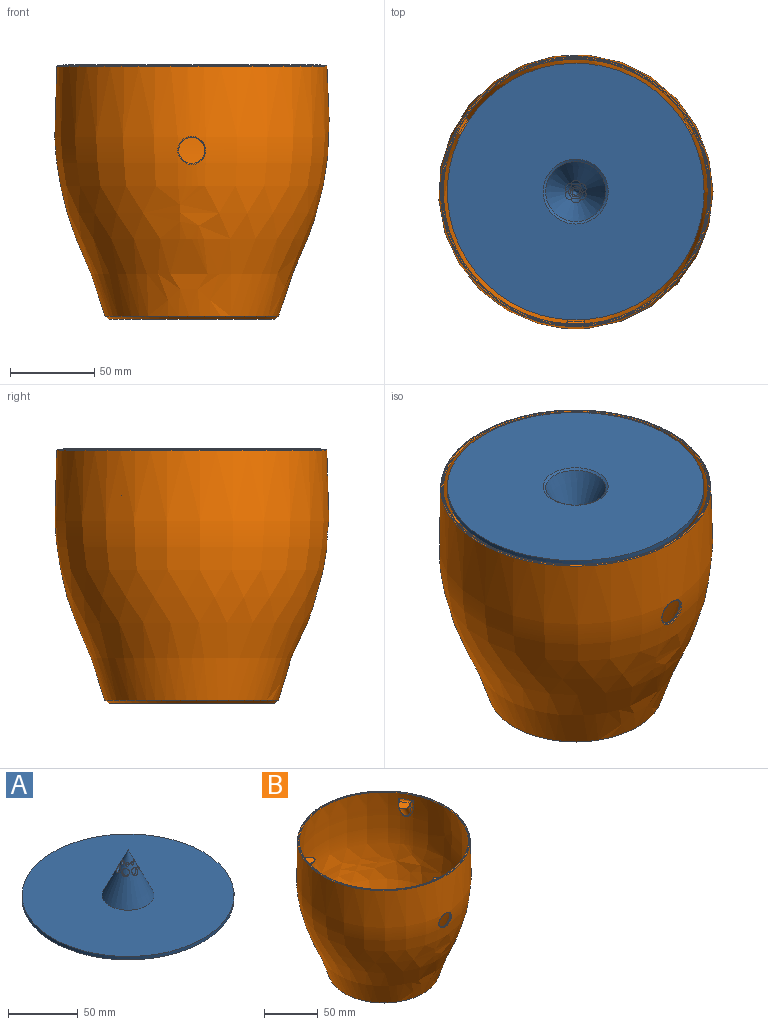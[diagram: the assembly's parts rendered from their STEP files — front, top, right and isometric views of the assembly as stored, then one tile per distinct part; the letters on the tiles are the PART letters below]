
ASSEMBLY  parts=2 mates=1
PART A: 25 faces, bbox 152x152x42.9 mm
  f0: cylinder r=2.75mm len=5.49mm, axis (0,1,0), area 15.8mm2, adj f1
  f1: cone r=18.55mm half-angle=25deg, axis (0,0,-1), area 27.1mm2, adj f0
  f2: cone r=18.55mm half-angle=25deg, axis (0,0,-1), area 2358.4mm2, adj f3
  f3: cone r=19.23mm half-angle=57.5deg, axis (0,0,-1), area 196.3mm2, adj f2,f4
  f4: plane 152.05x152.05mm, normal (0,0,1), area 16994.9mm2, adj f3,f5
  f5: cylinder r=76.02mm len=152.05mm, axis (0,0,-1), area 1433mm2, adj f4,f6
  f6: plane 152.05x152.05mm, normal (0,0,-1), area 17070.2mm2, adj f5,f7
  f7: cone r=20mm half-angle=25deg, axis (0,0,-1), area 2373.6mm2, adj f6,f8,f9,f13,f14,f15,f16,f17
  f8: cylinder r=2.75mm len=5.49mm, axis (0,1,0), area 48mm2, adj f7
  f9: cylinder r=2.75mm len=6.92mm, axis (-0.87,0.5,0), area 31.3mm2, adj f7,f10,f11,f12,f14
  f10: cone r=18.55mm half-angle=25deg, axis (0,0,-1), area 294.3mm2, adj f9,f11,f13,f14,f15,f16
  f11: cylinder r=2.75mm len=5.49mm, axis (0,1,0), area 16.5mm2, adj f9,f10,f12,f13
  f12: cone r=18.55mm half-angle=25deg, axis (0,0,-1), area 61.3mm2, adj f9,f11,f13,f14,f15,f16,f17,f19
  f13: cylinder r=2.75mm len=6.92mm, axis (-0.87,-0.5,0), area 31.3mm2, adj f7,f10,f11,f12,f16
  f14: cylinder r=2.75mm len=6.93mm, axis (-0.87,-0.5,0), area 31.4mm2, adj f7,f9,f10,f12,f15
  f15: cylinder r=2.75mm len=5.49mm, axis (0,-1,0), area 31.3mm2, adj f7,f10,f12,f14,f16
  f16: cylinder r=2.75mm len=6.92mm, axis (0.87,-0.5,0), area 31.3mm2, adj f7,f10,f12,f13,f15
  f17: cylinder r=1.25mm len=2.92mm, axis (0,1,0), area 14mm2, adj f7,f12,f18,f19,f20
  f18: cone r=18.55mm half-angle=25deg, axis (0,0,-1), area 34.9mm2, adj f17,f19,f20,f21,f22,f23,f24
  f19: cylinder r=1.25mm len=3.85mm, axis (-0.78,0.62,0), area 14mm2, adj f7,f12,f17,f18,f24
  f20: cylinder r=1.25mm len=3.85mm, axis (0.78,0.62,0), area 13.9mm2, adj f7,f12,f17,f18,f23
  f21: cylinder r=1.25mm len=3.72mm, axis (-0.43,-0.9,0), area 14mm2, adj f7,f12,f18,f22,f24
  f22: cylinder r=1.25mm len=3.72mm, axis (0.43,-0.9,0), area 14mm2, adj f7,f12,f18,f21,f23
  f23: cylinder r=1.25mm len=3.41mm, axis (0.97,-0.22,0), area 13.9mm2, adj f7,f12,f18,f20,f22
  f24: cylinder r=1.25mm len=3.43mm, axis (-0.97,-0.22,0), area 14mm2, adj f7,f12,f18,f19,f21
PART B: 39 faces, bbox 173.3x173.3x150 mm
  f0: revolved ~159.5x159.5mm, area 119611.4mm2, adj f21,f22,f23,f24,f25,f26,f27,f28
  f1: revolved ~162.68x162.68mm, area 69001.8mm2, adj f18,f19,f20
  f2: plane 97.7x97.7mm, normal (0,0,-1), area 7496.5mm2, adj f19
  f3: plane 159.07x159.07mm, normal (0,0,1), area 299.5mm2, adj f17,f18
  f4: cylinder r=7.75mm len=15.5mm, axis (0,1,0), area 29.4mm2, adj f20,f21
  f5: plane 10.71x10mm, normal (0,0,1), area 92.9mm2, adj f6,f7,f8,f31,f32,f33
  f6: plane 5.68x4.46mm, normal (1,0,0), area 11.8mm2, adj f5,f8,f32
  f7: plane 5.68x4.46mm, normal (-1,0,0), area 11.8mm2, adj f5,f8,f31
  f8: cylinder r=5mm len=19.8mm, axis (0,-0.62,-0.79), area 253mm2, adj f5,f6,f7,f30
  f9: plane 12.18x11.8mm, normal (0,0,1), area 92.9mm2, adj f10,f11,f12,f27,f28,f29
  f10: plane 5.68x3.86mm, normal (-0.5,0.87,0), area 11.8mm2, adj f9,f12,f28
  f11: plane 5.68x3.86mm, normal (0.5,-0.87,0), area 11.8mm2, adj f9,f12,f27
  f12: cylinder r=5mm len=19.8mm, axis (0.53,0.31,-0.79), area 253mm2, adj f9,f10,f11,f26
  f13: plane 12.18x11.8mm, normal (0,0,1), area 92.9mm2, adj f14,f15,f16,f23,f24,f25
  f14: plane 5.68x3.86mm, normal (-0.5,-0.87,0), area 11.8mm2, adj f13,f16,f24
  f15: plane 5.68x3.86mm, normal (0.5,0.87,0), area 11.8mm2, adj f13,f16,f23
  f16: cylinder r=5mm len=19.8mm, axis (-0.53,0.31,-0.79), area 253mm2, adj f13,f14,f15,f22
  f17: torus R=78.93mm, axis (0,0,1), area 405.9mm2, adj f3
  f18: torus R=79.54mm, axis (0,0,1), area 375.8mm2, adj f1,f3
  f19: cone r=51.43mm half-angle=53.4deg, axis (0,0,1), area 1011.9mm2, adj f1,f2
  f20: bspline ~16.63x16.55mm, area 41.1mm2, adj f1,f4
  f21: bspline ~16.48x16.41mm, area 37.3mm2, adj f0,f4
  f22: bspline ~14.57x12.47mm, area 64.1mm2, adj f0,f16,f23,f24
  f23: bspline ~23.78x3.41mm, area 21.3mm2, adj f0,f13,f15,f22,f25
  f24: bspline ~23.78x3.73mm, area 21.3mm2, adj f0,f13,f14,f22,f25
  f25: torus R=76.88mm, axis (0,0,1), area 38mm2, adj f0,f13,f23,f24
  f26: bspline ~14.57x12.46mm, area 64.1mm2, adj f0,f12,f27,f28
  f27: bspline ~23.78x3.73mm, area 21.3mm2, adj f0,f9,f11,f26,f29
  f28: bspline ~23.78x3.41mm, area 21.3mm2, adj f0,f9,f10,f26,f29
  f29: torus R=76.88mm, axis (0,0,1), area 38mm2, adj f0,f9,f27,f28
  f30: bspline ~14.57x14.36mm, area 64.1mm2, adj f0,f8,f31,f32
  f31: bspline ~23.78x3.25mm, area 21.3mm2, adj f0,f5,f7,f30,f33
  f32: bspline ~23.78x3.25mm, area 21.3mm2, adj f0,f5,f6,f30,f33
  f33: torus R=76.88mm, axis (0,0,1), area 38mm2, adj f0,f5,f31,f32
  f34: plane 109.03x109.03mm, normal (0,0,1), area 7815.5mm2, adj f37,f38
  f35: cylinder r=20mm len=40mm, axis (0,0,1), area 2261.9mm2, adj f36,f37
  f36: plane 40x40mm, normal (0,0,1), area 1256.6mm2, adj f35
  f37: torus R=22mm, axis (0,0,1), area 409.1mm2, adj f34,f35
  f38: torus R=54.51mm, axis (0,0,1), area 855.5mm2, adj f0,f34
PLACE A rot(axis=(1,0,0),180deg) t=(-146.73,-45.31,141.29)mm
PLACE B t=(-146.73,-45.31,-9.45)mm
MATE cylindrical A.f1 <-> B.f17  axis (0,0,1) through (-146.73,-45.31,141.29)mm
